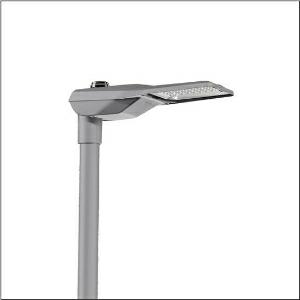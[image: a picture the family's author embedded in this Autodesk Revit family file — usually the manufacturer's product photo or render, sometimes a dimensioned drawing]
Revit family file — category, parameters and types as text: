
# Revit family: streetlight_sl_21_mini___st1_0a_5xe6d57n08hb_5f9a
name_source: partatom
category: Lighting Fixtures
units: mm (PartAtom-declared; Revit-internal decimal feet)

## family parameters
Cut with Voids When Loaded = No
Host = Face
Light Source = No
Part Type = Normal
Room Calculation Point = No
Round Connector Dimension = Use Diameter
Shared = No

## types (1)
- --- (1 x LED, 7780 lm, 66 W, 3000K)
    Apparent Load = 66 VA
    CIE Flux Codes = 37 72 97 100 100
    Color Rendering = 80
    Color Temperature = 3000K
    Default Elevation = 1800 mm
    Description = Streetlight SL 21 mini, mast luminaire, primary light control with lens, of PMMA, primary optical cover: cover, of toughened safety glass, transparent, light distribution: ST1.0a, light emission: direct distribution, primary light characteristic: asymmetric, installation type: side-entry, LED, 3G 1.5mm², High Power LED, rated luminous flux: 7.780lm, luminous efficacy: 118lm/W, light colour: 830, colour temperature: 3000K, control gear: NEMA (7pin), control: overheat protection, pre-setting: linear dimming characteristic, constant luminous flux control, time-dependent luminous flux control, flexible luminous flux parameterisation, mains connection: 230..240V, AC, 50/60Hz, connection cable pre-assembled, cable length: 8,5m, wiring characteristics: H07RN-F, start of lifetime: 66W, end of service life: 69W, reduction: 30W, luminaire housing, of diecast aluminium (EN AC-44300), powder-coated, SITECO metallic grey (DB 702S), corrosivity category C5 high according to DIN EN ISO 12944, multi-level sealing system, sealing non-destructively replaceable, inclination adjustable: 0°, 5°, 10°, 15°, length: 628mm, width: 235mm, height: 110mm, spigot size: 42mm (side-entry), mounting height: 4..8m, protection rating (complete): IP66, insulation class (complete): insulation class I (protective earthing), certification: CE, ENEC, ENEC+, VDE, impact resistance: IK10, permissible operating ambient temperature for outdoor applications: -40..+50°C, standard-compliant lighting for roads and squares, packaging unit: 1 piece

Light Distribution: ST1.0a
    Height = 110 mm
    Lamp = 1 x LED
    Lamp Light Flux = 7780 lm
    Lamp Power = 66 W
    Lamp count = 1
    Length = 625 mm
    Luminous efficacy = 118 lm/W
    Manufacturer = Siteco
    ModVariant = No
    Model = 5XE6D57N08HB
    Number of Poles = 1
    OnlyDefault = Yes
    Power Factor = 1
    Product Name = Streetlight SL 21 mini | ST1.0a
    Product group = mast luminaire | pylon top
    ProductGroupID = 6100
    Protection Class = Protection class I
    Protection Degree = IP 66
    RLX_Detail_Level = 1
    RLX_Emergency_Light_Flux = 0 lm
    RLX_Emergency_Type = 0
    RLX_Emergency_Type_DB = No
    RlxData = <blob elided: 26189 chars, md5=229b6821>
    Socket = socket
    Standby Power = 0 W
    System Light Flux = 7780 lm
    System Power = 66 W
    Type Comments = factory setting: luminous flux: 100 % | dim-lin: 254 | 670 mA
    Type Image = l_1294379.jpg
    URL = http://relux.com
    VarID = @adj_135659
    Voltage = 0 V
    Weight = 0.00 kg
    Width = 234 mm

## geometry (parser evidence)
native form markers: Blend x4, Sweep x12
no freeform markers — native parametric forms only
